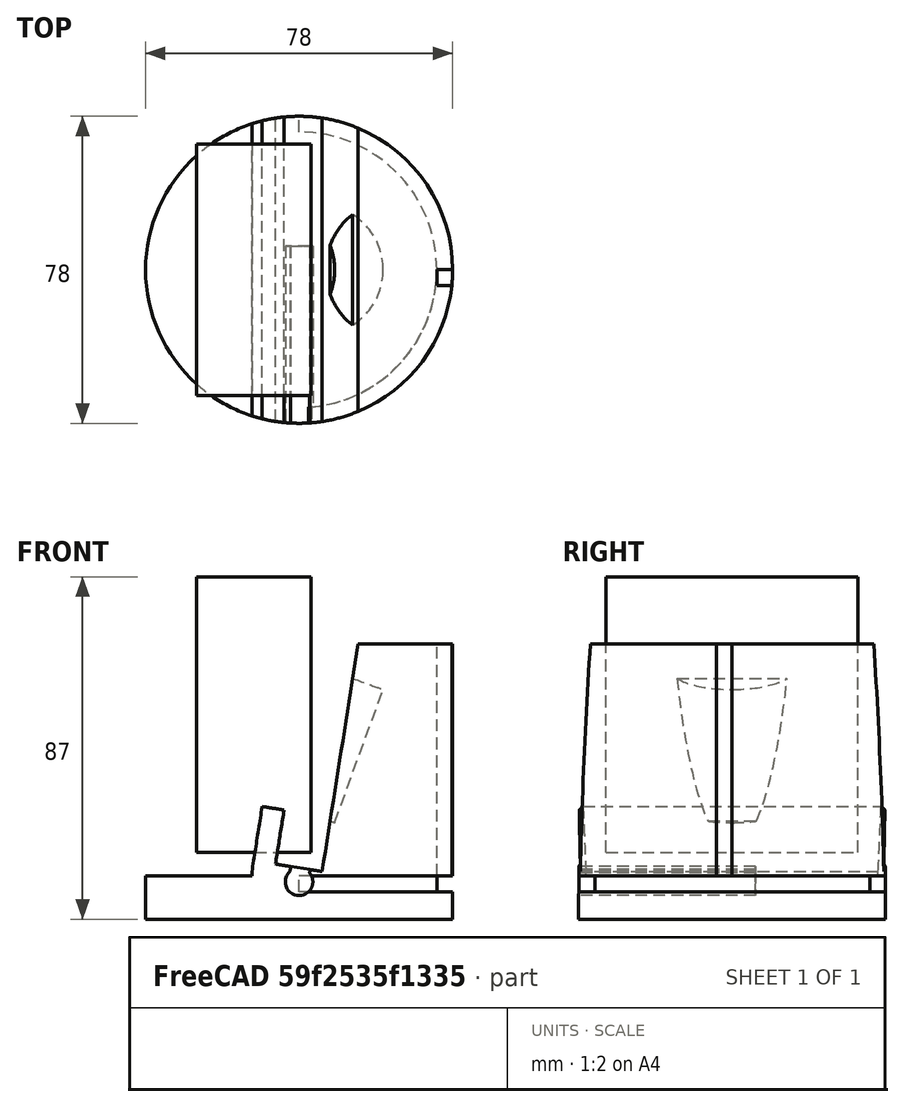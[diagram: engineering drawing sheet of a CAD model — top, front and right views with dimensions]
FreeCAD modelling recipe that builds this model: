
FCSTD DOCUMENT  (FreeCAD 0.18R4 (GitTag))
Label: phone_cup_holder
License: All rights reserved
LicenseURL: http://en.wikipedia.org/wiki/All_rights_reserved
objects: Part::Box×7, Part::Cylinder×5, Part::MultiFuse×4, Part::Cut×2
note: 18 computed .brp shape members not serialized (recipe doc carries the construction recipe); baked Part::Feature solids carry a one-line shape summary decoded from their .brp

FEATURE [Part::Cylinder] Cylinder  label="bot_cyl_body"
  Angle = 360
  AttacherType = Attacher::AttachEngine3D
  Height = 70
  Radius = 39
FEATURE [Part::Box] Box  label="phone_model"
  AttacherType = Attacher::AttachEngine3D
  Height = 150
  Length = 12
  Placement = pos=(-6,-39,14) rot=(0,1,0;0.15708rad)
  Width = 78
FEATURE [Part::Box] Box001  label="front_hole"
  AttacherType = Attacher::AttachEngine3D
  Height = 150
  Length = 12
  Placement = pos=(-24,-39,13) rot=(0,1,0;0.15708rad)
  Width = 78
FEATURE [Part::Box] Box002  label="front_hole_big"
  AttacherType = Attacher::AttachEngine3D
  Height = 150
  Length = 29
  Placement = pos=(-41,-39,11) rot=(0,1,0;0rad)
  Width = 78
FEATURE [Part::Box] Box003  label="front_hole_small"
  AttacherType = Attacher::AttachEngine3D
  Height = 70
  Length = 29
  Placement = pos=(-26,-32,17) rot=(0,1,0;0rad)
  Width = 64
FEATURE [Part::Cylinder] Cylinder001  label="Cylinder"
  Angle = 360
  AttacherType = Attacher::AttachEngine3D
  Height = 47
  Placement = pos=(0,6,9.5) rot=(1,0,0;1.5708rad)
  Radius = 3.5
FEATURE [Part::Cylinder] Cylinder002  label="cord_hole"
  Angle = 180
  AttacherType = Attacher::AttachEngine3D
  Height = 4
  Placement = pos=(0,0,0) rot=(0,0,-1;1.5708rad)
  Radius = 39
FEATURE [Part::Cylinder] Cylinder003  label="cord_hole_inner"
  Angle = 360
  AttacherType = Attacher::AttachEngine3D
  Height = 4
  Radius = 35
FEATURE [Part::Box] Box004  label="Cube"
  AttacherType = Attacher::AttachEngine3D
  Height = 83
  Length = 4
  Placement = pos=(35,-4,0) rot=(0,0,1;0rad)
  Width = 4
FEATURE [Part::MultiFuse] Fusion001
  Shapes = -> [Cylinder002,Box004]
FEATURE [Part::Box] Box005  label="plug_cube"
  AttacherType = Attacher::AttachEngine3D
  Height = 10
  Length = 5
  Placement = pos=(-2.5,-39,11) rot=(0,1,0;0.15708rad)
  Width = 45
FEATURE [Part::Cut] Cut001  label="cord_track"
  Base = -> Fusion001
  Placement = pos=(0,0,7) rot=(0,0,1;0rad)
  Tool = -> Cylinder003
FEATURE [Part::MultiFuse] Fusion002  label="cord_track001"
  Shapes = -> [Cut001,Cylinder001,Box005]
FEATURE [Part::Cylinder] Cylinder004  label="grab_hole"
  Angle = 360
  AttacherType = Attacher::AttachEngine3D
  Height = 36
  Placement = pos=(-6,0,30) rot=(0,1,0;0.349066rad)
  Radius = 16
FEATURE [Part::Box] Box006  label="arm_cutter"
  AttacherType = Attacher::AttachEngine3D
  Height = 44
  Length = 20
  Placement = pos=(-18,-40,30) rot=(0,1,0;0.15708rad)
  Width = 79
FEATURE [Part::MultiFuse] Fusion  label="holes"
  Shapes = -> [Cylinder004,Box006,Box,Box001,Box002]
FEATURE [Part::MultiFuse] Fusion003  label="negative"
  Shapes = -> [Fusion002,Fusion]
FEATURE [Part::Cut] Cut
  Base = -> Cylinder
  Tool = -> Fusion003
